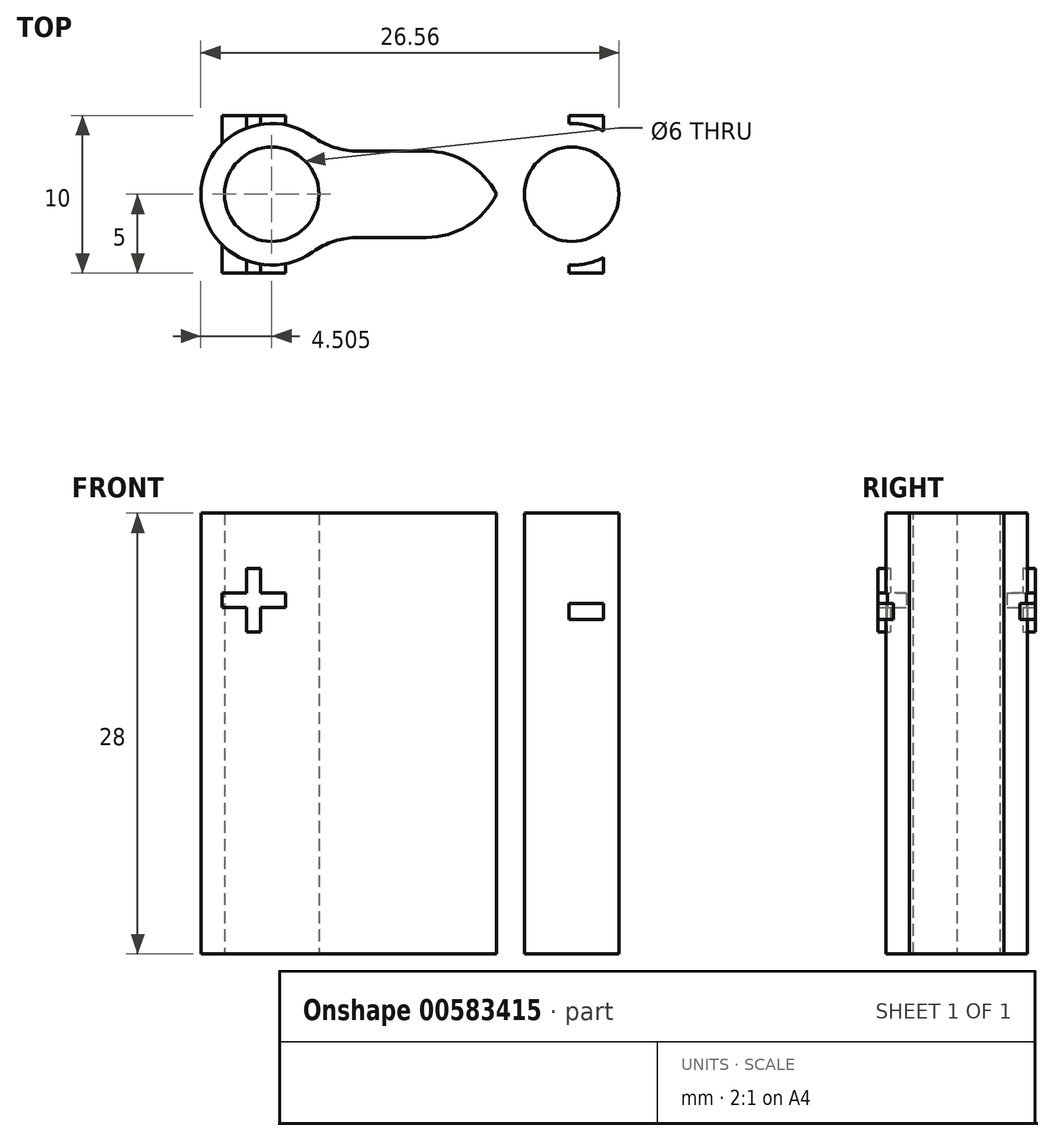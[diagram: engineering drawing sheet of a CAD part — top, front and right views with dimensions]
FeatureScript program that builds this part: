
annotation { "Feature Type Name" : "Feature", "Feature Type Description" : "" }
export const myFeature = defineFeature(function(context is Context, id is Id, definition is map)
    precondition{}
    {
        {
            var Q0;
            Q0=qCreatedBy(makeId("Top.planeOp"),FACE);
            var sketch = newSketch(context, id + "F0", { "sketchPlane" : qUnion([Q0])});
            skCircle(sketch, "E0", {"center": v(-9.53, 0) * mm, "radius": 3 * mm});
            skCircle(sketch, "E1.MirrorC", {"center": v(9.53, 0) * mm, "radius": 3 * mm});
            skCircle(sketch, "E2", {"center": v(-9.53, 0) * mm, "radius": 4.5 * mm});
            skCircle(sketch, "E3.MirrorC", {"center": v(9.53, 0) * mm, "radius": 4.5 * mm});
            skLineSegment(sketch, "E4", {"start": v(-5.96, 2.74) * mm, "end": v(5.96, 2.74) * mm});
            skLineSegment(sketch, "E5.MirrorCS", {"start": v(-5.96, -2.74) * mm, "end": v(5.96, -2.74) * mm});
            skSolve(sketch);
        }
        {
            var Q0;
            Q0=makeQuery(id+"F0.imprint","IMPRINT",FACE,{"disambiguationData":[TD([[makeQuery(id+"F0.imprint","IMPRINT",EDGE,{"derivedFrom":sQuery(id+"F0.wireOp",EDGE,"E0")}),-1.0]])]});
            var Q1;
            {var subQ0=sQuery(id+"F0.wireOp",EDGE,"E4");Q1=makeQuery(id+"F0.imprint","IMPRINT",FACE,{"disambiguationData":[TD([[makeQuery(id+"F0.imprint","IMPRINT",EDGE,{"derivedFrom":subQ0}),-1.0]])]});}
            var Q2;
            Q2=makeQuery(id+"F0.imprint","IMPRINT",FACE,{"disambiguationData":[TD([[makeQuery(id+"F0.imprint","IMPRINT",EDGE,{"derivedFrom":sQuery(id+"F0.wireOp",EDGE,"E1.MirrorC")}),1.0]])]});
            extrude(context, id + "F1", {"entities" : qUnion([Q0, Q1, Q2]), "depth" : 28 * mm, "offsetDistance" : 25 * mm});
        }
        {
            var Q0;
            Q0=makeQuery(id+"F1.opExtrude","SWEPT_EDGE",EDGE,{"disambiguationData":[OSD([sQuery(id+"F0.wireOp",EDGE,"E2"),sQuery(id+"F0.wireOp",EDGE,"E4")])]});
            var Q1;
            Q1=makeQuery(id+"F1.opExtrude","SWEPT_EDGE",EDGE,{"disambiguationData":[OSD([sQuery(id+"F0.wireOp",EDGE,"E3.MirrorC"),sQuery(id+"F0.wireOp",EDGE,"E4")])]});
            var Q2;
            Q2=makeQuery(id+"F1.opExtrude","SWEPT_EDGE",EDGE,{"disambiguationData":[OSD([sQuery(id+"F0.wireOp",EDGE,"E3.MirrorC"),sQuery(id+"F0.wireOp",EDGE,"E5.MirrorCS")])]});
            var Q3;
            Q3=makeQuery(id+"F1.opExtrude","SWEPT_EDGE",EDGE,{"disambiguationData":[OSD([sQuery(id+"F0.wireOp",EDGE,"E2"),sQuery(id+"F0.wireOp",EDGE,"E5.MirrorCS")])]});
            fillet(context, id + "F2", {"entities" : qUnion([Q0, Q1, Q2, Q3]), "radius" : 5 * mm, "tangentPropagation" : true, "allowEdgeOverflow" : false});
        }
        {
            var Q0;
            Q0=qCreatedBy(makeId("Front.planeOp"),FACE);
            var sketch = newSketch(context, id + "F3", { "sketchPlane" : qUnion([Q0])});
            skText(sketch, "E6", { "text": "+\n", "fontName": "OpenSans-Bold.ttf"});
            skText(sketch, "E7", { "text": "-", "fontName": "OpenSans-Bold.ttf"});
            const initialGuessF3  = {"E6": [-0.01305, 0.01953, 1, 0, 0.006], "E7": [0.0091, 0.01953, 1, 0, 0.006]};
            skSetInitialGuess(sketch, initialGuessF3);
            skSolve(sketch);
        }
        {
            var Q0;
            Q0 = qSketchRegion(id + "F3", true);
            extrude(context, id + "F4", {"entities" : qUnion([Q0]), "operationType" : NewBodyOperationType.ADD, "endBound" : BoundingType.SYMMETRIC, "depth" : 10 * mm, "offsetDistance" : 25 * mm});
        }
        {
            var Q0;
            Q0=makeQuery(id+"F0.imprint","IMPRINT",FACE,{"disambiguationData":[TD([[makeQuery(id+"F0.imprint","IMPRINT",EDGE,{"derivedFrom":sQuery(id+"F0.wireOp",EDGE,"E1.MirrorC")}),-1.0]])]});
            var Q1;
            Q1=makeQuery(id+"F0.imprint","IMPRINT",FACE,{"disambiguationData":[TD([[makeQuery(id+"F0.imprint","IMPRINT",EDGE,{"derivedFrom":sQuery(id+"F0.wireOp",EDGE,"E0")}),1.0]])]});
            extrude(context, id + "F5", {"entities" : qUnion([Q0, Q1]), "operationType" : NewBodyOperationType.REMOVE, "depth" : 25 * mm, "offsetDistance" : 25 * mm});
        }
    });
